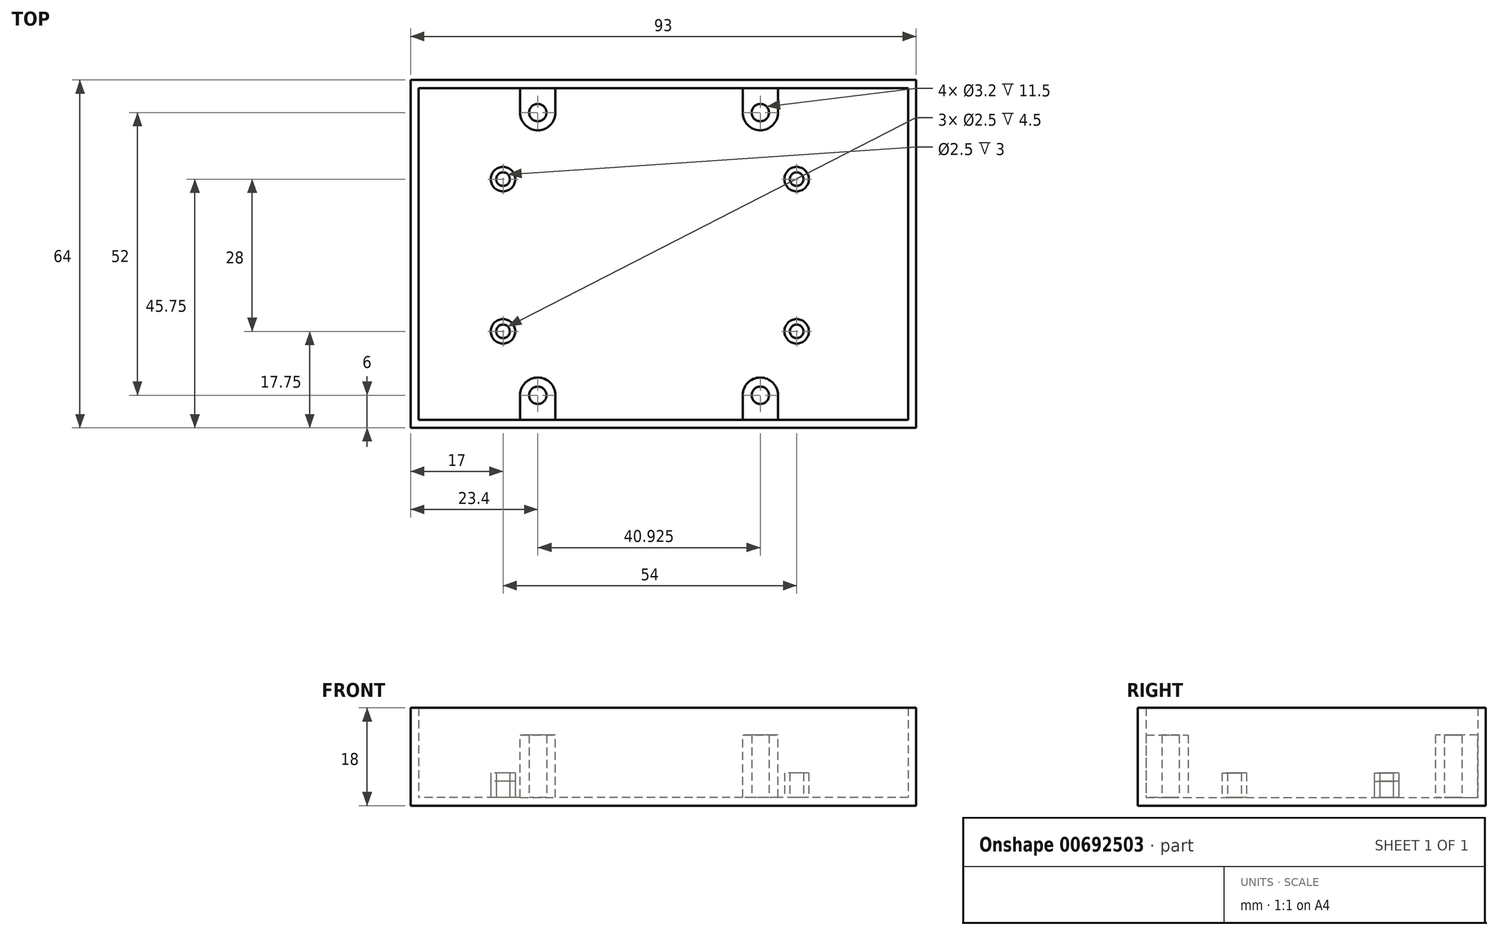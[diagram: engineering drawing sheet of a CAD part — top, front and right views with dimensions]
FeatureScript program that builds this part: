
annotation { "Feature Type Name" : "Feature", "Feature Type Description" : "" }
export const myFeature = defineFeature(function(context is Context, id is Id, definition is map)
    precondition{}
    {
        {
            var Q0;
            Q0=qCreatedBy(makeId("Top.planeOp"),FACE);
            var sketch = newSketch(context, id + "F0", { "sketchPlane" : qUnion([Q0])});
            skLineSegment(sketch, "E0.bottom", {"start": v(46.5, -32) * mm, "end": v(-46.5, -32) * mm});
            skLineSegment(sketch, "E0.top", {"start": v(46.5, 32) * mm, "end": v(-46.5, 32) * mm});
            skLineSegment(sketch, "E0.left", {"start": v(46.5, -32) * mm, "end": v(46.5, 32) * mm});
            skLineSegment(sketch, "E0.right", {"start": v(-46.5, -32) * mm, "end": v(-46.5, 32) * mm});
            skPoint(sketch, "E0.middle", {"position": v(0, 0) * mm});
            skSolve(sketch);
        }
        {
            var Q0;
            Q0 = qSketchRegion(id + "F0", true);
            extrude(context, id + "F1", {"entities" : qUnion([Q0]), "depth" : 18 * mm, "offsetDistance" : 25 * mm});
        }
        {
            var Q0;
            Q0=makeQuery(id+"F1.opExtrude","CAP_FACE",FACE,{"disambiguationData":[OSD([sQuery(id+"F0.wireOp",EDGE,"E0.bottom"),sQuery(id+"F0.wireOp",EDGE,"E0.top"),sQuery(id+"F0.wireOp",EDGE,"E0.left"),sQuery(id+"F0.wireOp",EDGE,"E0.right")])],"isStart":false});
            shell(context, id + "F2", {"entities" : qUnion([Q0]), "thickness" : 1.5 * mm});
        }
        {
            var Q0;
            Q0=qCreatedBy(makeId("Top.planeOp"),FACE);
            var sketch = newSketch(context, id + "F3", { "sketchPlane" : qUnion([Q0])});
            skCircle(sketch, "E1", {"center": v(-29.5, 13.75) * mm, "radius": 2.25 * mm});
            skCircle(sketch, "E2", {"center": v(24.5, 13.75) * mm, "radius": 2.25 * mm});
            skCircle(sketch, "E3", {"center": v(24.5, -14.25) * mm, "radius": 2.25 * mm});
            skCircle(sketch, "E4", {"center": v(-29.5, -14.25) * mm, "radius": 2.25 * mm});
            skLineSegment(sketch, "E5.bottom", {"start": v(-29.5, 13.75) * mm, "end": v(24.5, 13.75) * mm, "construction": true});
            skLineSegment(sketch, "E5.top", {"start": v(-29.5, -14.25) * mm, "end": v(24.5, -14.25) * mm, "construction": true});
            skLineSegment(sketch, "E5.left", {"start": v(-29.5, 13.75) * mm, "end": v(-29.5, -14.25) * mm, "construction": true});
            skLineSegment(sketch, "E5.right", {"start": v(24.5, 13.75) * mm, "end": v(24.5, -14.25) * mm, "construction": true});
            skLineSegment(sketch, "E6.bottom", {"start": v(-44, 31) * mm, "end": v(44, 31) * mm, "construction": true});
            skLineSegment(sketch, "E6.top", {"start": v(-44, -31) * mm, "end": v(44, -31) * mm, "construction": true});
            skLineSegment(sketch, "E6.left", {"start": v(-44, 31) * mm, "end": v(-44, -31) * mm, "construction": true});
            skLineSegment(sketch, "E6.right", {"start": v(44, 31) * mm, "end": v(44, -31) * mm, "construction": true});
            skPoint(sketch, "E6.middle", {"position": v(0, 0) * mm});
            skCircle(sketch, "E7", {"center": v(-29.5, 13.75) * mm, "radius": 1.25 * mm});
            skCircle(sketch, "E8", {"center": v(-29.5, -14.25) * mm, "radius": 1.25 * mm});
            skCircle(sketch, "E9", {"center": v(24.5, -14.25) * mm, "radius": 1.25 * mm});
            skCircle(sketch, "E10", {"center": v(24.5, 13.75) * mm, "radius": 1.25 * mm});
            skLineSegment(sketch, "E11.bottom", {"start": v(14.57, 31) * mm, "end": v(21.07, 31) * mm});
            skLineSegment(sketch, "E11.left", {"start": v(14.57, 31) * mm, "end": v(14.57, 26) * mm});
            skLineSegment(sketch, "E11.right", {"start": v(21.07, 31) * mm, "end": v(21.07, 26) * mm});
            skLineSegment(sketch, "E12.bottom", {"start": v(-26.35, 31) * mm, "end": v(-19.85, 31) * mm});
            skLineSegment(sketch, "E12.left", {"start": v(-26.35, 31) * mm, "end": v(-26.35, 26) * mm});
            skLineSegment(sketch, "E12.right", {"start": v(-19.85, 31) * mm, "end": v(-19.85, 26) * mm});
            skLineSegment(sketch, "E13.bottom", {"start": v(-26.35, -31) * mm, "end": v(-19.85, -31) * mm});
            skLineSegment(sketch, "E13.left", {"start": v(-26.35, -31) * mm, "end": v(-26.35, -26) * mm});
            skLineSegment(sketch, "E13.right", {"start": v(-19.85, -31) * mm, "end": v(-19.85, -26) * mm});
            skLineSegment(sketch, "E14.bottom", {"start": v(14.57, -31) * mm, "end": v(21.07, -31) * mm});
            skLineSegment(sketch, "E14.left", {"start": v(14.57, -31) * mm, "end": v(14.57, -26) * mm});
            skLineSegment(sketch, "E14.right", {"start": v(21.07, -31) * mm, "end": v(21.07, -26) * mm});
            skArc(sketch, "E15", {"start": v(-26.35, 26) * mm, "mid": v(-23.1, 22.75) * mm, "end": v(-19.85, 26) * mm});
            skArc(sketch, "E16", {"start": v(14.57, 26) * mm, "mid": v(17.82, 22.75) * mm, "end": v(21.07, 26) * mm});
            skArc(sketch, "E17", {"start": v(21.08, -26) * mm, "mid": v(17.82, -22.75) * mm, "end": v(14.57, -26) * mm});
            skArc(sketch, "E18", {"start": v(-19.85, -26) * mm, "mid": v(-23.1, -22.75) * mm, "end": v(-26.35, -26) * mm});
            skCircle(sketch, "E19", {"center": v(-23.1, 26) * mm, "radius": 1.6 * mm});
            skCircle(sketch, "E20", {"center": v(17.82, 26) * mm, "radius": 1.6 * mm});
            skCircle(sketch, "E21", {"center": v(17.82, -26) * mm, "radius": 1.6 * mm});
            skCircle(sketch, "E22", {"center": v(-23.1, -26) * mm, "radius": 1.6 * mm});
            skSolve(sketch);
        }
        {
            var Q0;
            Q0=makeQuery(id+"F3.imprint","IMPRINT",FACE,{"disambiguationData":[TD([[makeQuery(id+"F3.imprint","IMPRINT",EDGE,{"derivedFrom":sQuery(id+"F3.wireOp",EDGE,"E4")}),1.0]])]});
            var Q1;
            Q1=makeQuery(id+"F3.imprint","IMPRINT",FACE,{"disambiguationData":[TD([[makeQuery(id+"F3.imprint","IMPRINT",EDGE,{"derivedFrom":sQuery(id+"F3.wireOp",EDGE,"E3")}),1.0]])]});
            var Q2;
            Q2=makeQuery(id+"F3.imprint","IMPRINT",FACE,{"disambiguationData":[TD([[makeQuery(id+"F3.imprint","IMPRINT",EDGE,{"derivedFrom":sQuery(id+"F3.wireOp",EDGE,"E2")}),1.0]])]});
            extrude(context, id + "F4", {"entities" : qUnion([Q0, Q1, Q2]), "operationType" : NewBodyOperationType.ADD, "depth" : 6 * mm, "offsetDistance" : 25 * mm});
        }
        {
            var Q0;
            Q0=makeQuery(id+"F3.imprint","IMPRINT",FACE,{"disambiguationData":[TD([[makeQuery(id+"F3.imprint","IMPRINT",EDGE,{"derivedFrom":sQuery(id+"F3.wireOp",EDGE,"E1")}),1.0]])]});
            extrude(context, id + "F5", {"entities" : qUnion([Q0]), "operationType" : NewBodyOperationType.ADD, "depth" : 4.5 * mm, "offsetDistance" : 25 * mm});
        }
        {
            var Q0;
            Q0=makeQuery(id+"F3.imprint","IMPRINT",FACE,{"disambiguationData":[TD([[makeQuery(id+"F3.imprint","IMPRINT",EDGE,{"derivedFrom":sQuery(id+"F3.wireOp",EDGE,"E12.bottom")}),-1.0]])]});
            var Q1;
            Q1=makeQuery(id+"F3.imprint","IMPRINT",FACE,{"disambiguationData":[TD([[makeQuery(id+"F3.imprint","IMPRINT",EDGE,{"derivedFrom":sQuery(id+"F3.wireOp",EDGE,"E11.bottom")}),-1.0]])]});
            var Q2;
            Q2=makeQuery(id+"F3.imprint","IMPRINT",FACE,{"disambiguationData":[TD([[makeQuery(id+"F3.imprint","IMPRINT",EDGE,{"derivedFrom":sQuery(id+"F3.wireOp",EDGE,"E14.bottom")}),1.0]])]});
            var Q3;
            Q3=makeQuery(id+"F3.imprint","IMPRINT",FACE,{"disambiguationData":[TD([[makeQuery(id+"F3.imprint","IMPRINT",EDGE,{"derivedFrom":sQuery(id+"F3.wireOp",EDGE,"E13.bottom")}),1.0]])]});
            extrude(context, id + "F6", {"entities" : qUnion([Q0, Q1, Q2, Q3]), "operationType" : NewBodyOperationType.ADD, "depth" : 13 * mm, "offsetDistance" : 25 * mm});
        }
    });
